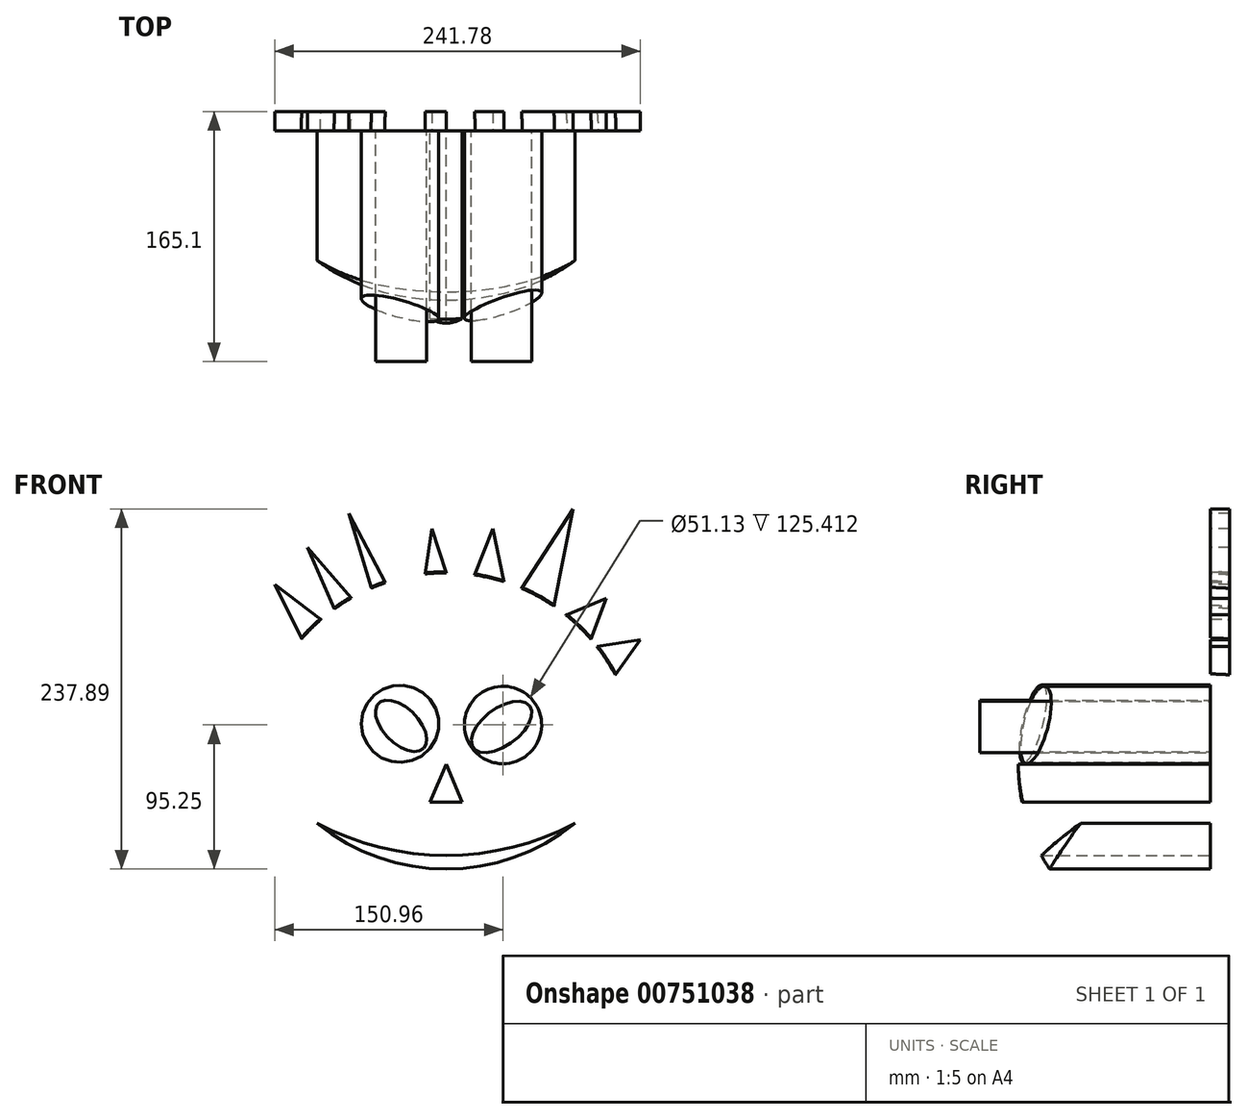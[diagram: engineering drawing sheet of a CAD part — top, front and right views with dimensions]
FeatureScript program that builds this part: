
annotation { "Feature Type Name" : "Feature", "Feature Type Description" : "" }
export const myFeature = defineFeature(function(context is Context, id is Id, definition is map)
    precondition{}
    {
        {
            var Q0;
            Q0=qCreatedBy(makeId("Front.planeOp"),FACE);
            var sketch = newSketch(context, id + "F0", { "sketchPlane" : qUnion([Q0])});
            skArc(sketch, "E0", {"start": v(-85.19, -39.1) * mm, "mid": v(0, -69.43) * mm, "end": v(85.19, -39.1) * mm});
            skArc(sketch, "E1", {"start": v(-85.19, -39.1) * mm, "mid": v(0, -60.35) * mm, "end": v(85.19, -39.1) * mm});
            skCircle(sketch, "E2", {"center": v(-30.42, 26.59) * mm, "radius": 25.57 * mm});
            skCircle(sketch, "E3", {"center": v(37.58, 25.82) * mm, "radius": 25.57 * mm});
            skLineSegment(sketch, "E4", {"start": v(0, 0) * mm, "end": v(-10.74, -25.3) * mm});
            skLineSegment(sketch, "E5", {"start": v(-10.74, -25.3) * mm, "end": v(10.74, -25.3) * mm});
            skLineSegment(sketch, "E6", {"start": v(10.74, -25.3) * mm, "end": v(0, 0) * mm});
            skSolve(sketch);
        }
        {
            var Q0;
            Q0=qCreatedBy(makeId("Front.planeOp"),FACE);
            var sketch = newSketch(context, id + "F1", { "sketchPlane" : qUnion([Q0])});
            skArc(sketch, "E7", {"start": v(0, 127) * mm, "mid": v(-127, 0) * mm, "end": v(0, -127) * mm});
            skLineSegment(sketch, "E8", {"start": v(0, -127) * mm, "end": v(0, 127) * mm});
            skSolve(sketch);
        }
        {
            var Q0;
            Q0 = qSketchRegion(id + "F1", true);
            var Q1;
            Q1=sQuery(id+"F1.wireOp",EDGE,"E8");
            revolve(context, id + "F2", {"surfaceOperationType" : NewSurfaceOperationType.NEW, "entities" : qUnion([Q0]), "axis" : qUnion([Q1]), "revolveType" : RevolveType.FULL});
        }
        {
            var Q0;
            Q0 = qSketchRegion(id + "F0", true);
            extrude(context, id + "F3", {"entities" : qUnion([Q0]), "operationType" : NewBodyOperationType.REMOVE, "depth" : 127 * mm, "offsetDistance" : 25.4 * mm});
        }
        {
            var Q0;
            Q0=qCreatedBy(makeId("Front.planeOp"),FACE);
            var sketch = newSketch(context, id + "F4", { "sketchPlane" : qUnion([Q0])});
            skEllipse(sketch, "E9", {"center": v(36.65, 24.55) * mm, "majorRadius": 23.24 * mm, "minorRadius": 12.31 * mm, "majorAxis": v(0.8, 0.6)});
            skEllipse(sketch, "E10", {"center": v(-29.74, 25.24) * mm, "majorRadius": 21.03 * mm, "minorRadius": 11.56 * mm, "majorAxis": v(0.7, -0.7)});
            skSolve(sketch);
        }
        {
            var Q0;
            Q0 = qSketchRegion(id + "F4", true);
            extrude(context, id + "F5", {"entities" : qUnion([Q0]), "operationType" : NewBodyOperationType.ADD, "depth" : 152.4 * mm, "offsetDistance" : 25.4 * mm});
        }
        {
            var Q0;
            Q0=qCreatedBy(makeId("Front.planeOp"),FACE);
            var sketch = newSketch(context, id + "F6", { "sketchPlane" : qUnion([Q0])});
            skLineSegment(sketch, "E11", {"start": v(-87.63, 67.24) * mm, "end": v(-113.38, 118.74) * mm});
            skLineSegment(sketch, "E12", {"start": v(-113.38, 118.74) * mm, "end": v(-64.74, 81.9) * mm});
            skLineSegment(sketch, "E13", {"start": v(-64.74, 81.9) * mm, "end": v(-91.56, 143.06) * mm});
            skLineSegment(sketch, "E14", {"start": v(-91.56, 143.06) * mm, "end": v(-39.34, 82.98) * mm});
            skLineSegment(sketch, "E15", {"start": v(-39.34, 82.98) * mm, "end": v(-64.38, 165.6) * mm});
            skLineSegment(sketch, "E16", {"start": v(-64.38, 165.6) * mm, "end": v(-20.39, 82.26) * mm});
            skLineSegment(sketch, "E17", {"start": v(-20.39, 82.26) * mm, "end": v(-9.3, 155.58) * mm});
            skLineSegment(sketch, "E18", {"start": v(-9.3, 155.58) * mm, "end": v(8.94, 99.43) * mm});
            skLineSegment(sketch, "E19", {"start": v(8.94, 99.43) * mm, "end": v(30.76, 155.58) * mm});
            skLineSegment(sketch, "E20", {"start": v(30.76, 155.58) * mm, "end": v(41.85, 103.72) * mm});
            skLineSegment(sketch, "E21", {"start": v(41.85, 103.72) * mm, "end": v(84.05, 168.46) * mm});
            skLineSegment(sketch, "E22", {"start": v(84.05, 168.46) * mm, "end": v(69.39, 94.42) * mm});
            skLineSegment(sketch, "E23", {"start": v(69.39, 94.42) * mm, "end": v(105.87, 109.44) * mm});
            skLineSegment(sketch, "E24", {"start": v(105.87, 109.44) * mm, "end": v(93.35, 76.54) * mm});
            skLineSegment(sketch, "E25", {"start": v(93.35, 76.54) * mm, "end": v(128.4, 82.26) * mm});
            skLineSegment(sketch, "E26", {"start": v(128.4, 82.26) * mm, "end": v(107.3, 52.58) * mm});
            skLineSegment(sketch, "E27", {"start": v(107.3, 52.58) * mm, "end": v(46.85, 74.4) * mm});
            skLineSegment(sketch, "E28", {"start": v(46.85, 74.4) * mm, "end": v(-12.16, 74.4) * mm});
            skLineSegment(sketch, "E29", {"start": v(-12.16, 74.4) * mm, "end": v(-87.63, 67.24) * mm});
            skSolve(sketch);
        }
        {
            var Q0;
            Q0 = qSketchRegion(id + "F6", true);
            extrude(context, id + "F7", {"entities" : qUnion([Q0]), "operationType" : NewBodyOperationType.ADD, "oppositeDirection" : true, "depth" : 12.7 * mm, "offsetDistance" : 25.4 * mm});
        }
    });
